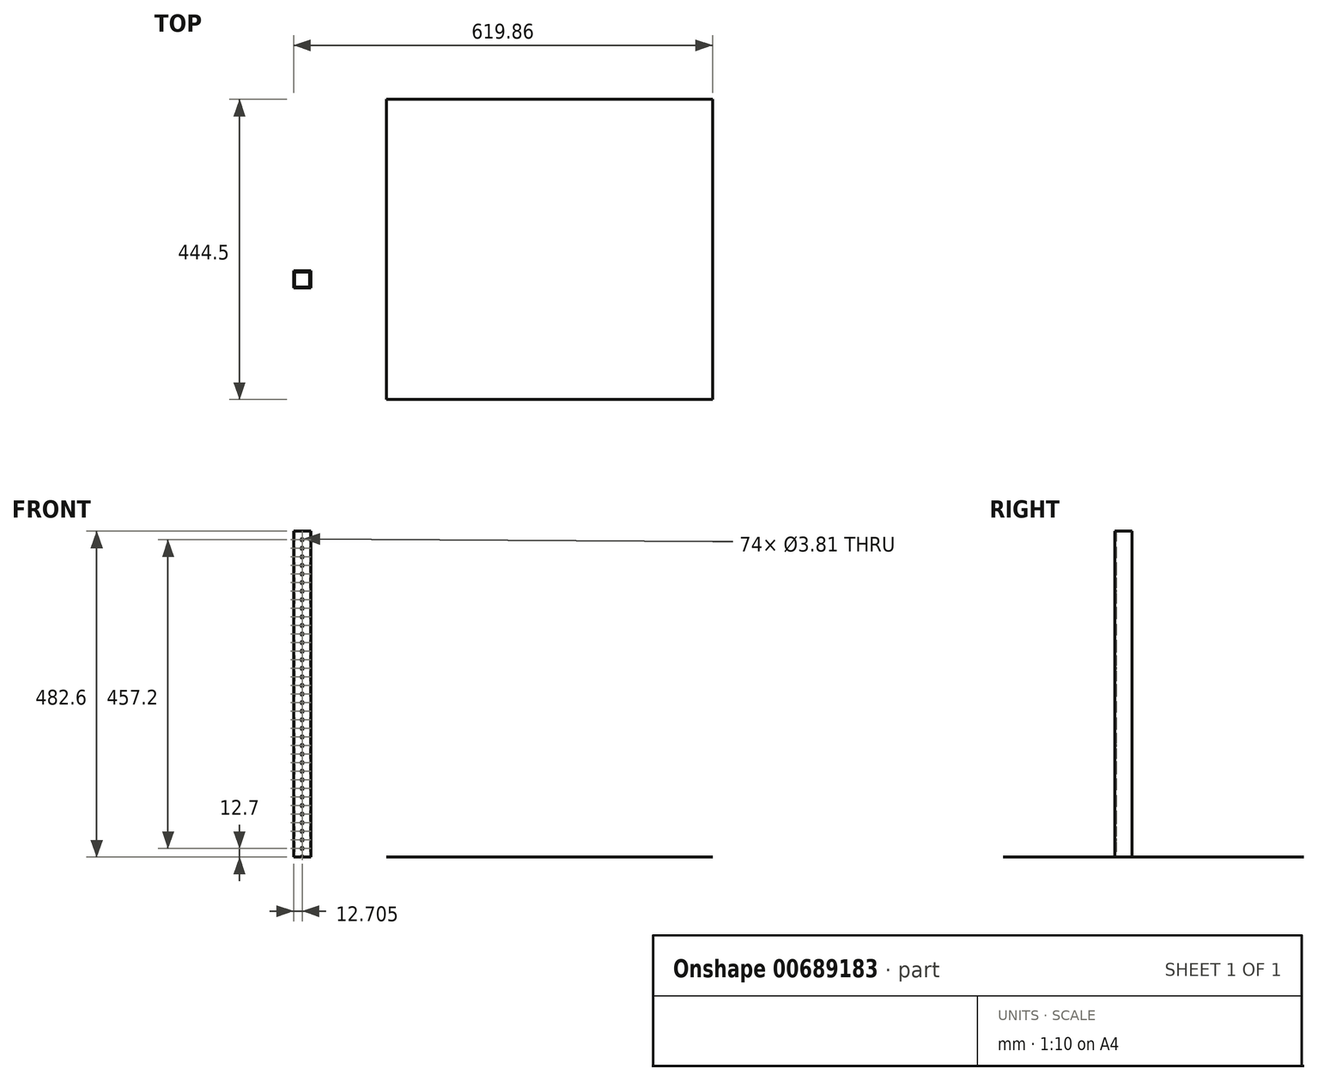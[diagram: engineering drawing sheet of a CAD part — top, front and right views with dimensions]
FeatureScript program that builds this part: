
annotation { "Feature Type Name" : "Feature", "Feature Type Description" : "" }
export const myFeature = defineFeature(function(context is Context, id is Id, definition is map)
    precondition{}
    {
        {
            var Q0;
            Q0=qCreatedBy(makeId("Top.planeOp"),FACE);
            var sketch = newSketch(context, id + "F0", { "sketchPlane" : qUnion([Q0])});
            skLineSegment(sketch, "E0.bottom", {"start": v(-66.34, 50.84) * mm, "end": v(-40.94, 50.84) * mm});
            skLineSegment(sketch, "E0.top", {"start": v(-66.34, 25.44) * mm, "end": v(-40.94, 25.44) * mm});
            skLineSegment(sketch, "E0.left", {"start": v(-66.34, 50.84) * mm, "end": v(-66.34, 25.44) * mm});
            skLineSegment(sketch, "E0.right", {"start": v(-40.94, 50.84) * mm, "end": v(-40.94, 25.44) * mm});
            skPoint(sketch, "E0.middle", {"position": v(-53.64, 38.14) * mm});
            skLineSegment(sketch, "E1.bottom", {"start": v(-64.75, 49.25) * mm, "end": v(-42.52, 49.25) * mm});
            skLineSegment(sketch, "E1.top", {"start": v(-64.75, 27.03) * mm, "end": v(-42.52, 27.03) * mm});
            skLineSegment(sketch, "E1.left", {"start": v(-64.75, 49.25) * mm, "end": v(-64.75, 27.03) * mm});
            skLineSegment(sketch, "E1.right", {"start": v(-42.52, 49.25) * mm, "end": v(-42.52, 27.03) * mm});
            skSolve(sketch);
        }
        {
            var Q0;
            Q0=makeQuery(id+"F0.imprint","IMPRINT",FACE,{"disambiguationData":[TD([[makeQuery(id+"F0.imprint","IMPRINT",EDGE,{"derivedFrom":sQuery(id+"F0.wireOp",EDGE,"E0.bottom")}),-1.0]])]});
            extrude(context, id + "F1", {"entities" : qUnion([Q0]), "depth" : 482.6 * mm, "offsetDistance" : 25.4 * mm});
        }
        {
            var Q0;
            Q0=makeQuery(id+"F1.opExtrude","SWEPT_FACE",FACE,{"disambiguationData":[OSD([sQuery(id+"F0.wireOp",EDGE,"E0.top")])]});
            var sketch = newSketch(context, id + "F2", { "sketchPlane" : qUnion([Q0])});
            skCircle(sketch, "E2", {"center": v(-53.64, 469.9) * mm, "radius": 1.9 * mm});
            skPoint(sketch, "E2.centerSnap0", {"position": v(-53.64, 482.6) * mm});
            skCircle(sketch, "E3.0.1.0", {"center": v(-53.64, 457.2) * mm, "radius": 1.9 * mm});
            skLineSegment(sketch, "E3.direction1", {"start": v(-53.64, 469.9) * mm, "end": v(-28.24, 469.9) * mm, "construction": true});
            skLineSegment(sketch, "E3.direction2", {"start": v(-53.64, 469.9) * mm, "end": v(-53.64, 457.2) * mm, "construction": true});
            skCircle(sketch, "E4.0.0.2", {"center": v(-53.64, 444.5) * mm, "radius": 1.9 * mm});
            skCircle(sketch, "E4.0.0.3", {"center": v(-53.64, 431.8) * mm, "radius": 1.9 * mm});
            skCircle(sketch, "E4.0.0.4", {"center": v(-53.64, 419.1) * mm, "radius": 1.9 * mm});
            skCircle(sketch, "E4.0.0.5", {"center": v(-53.64, 406.4) * mm, "radius": 1.9 * mm});
            skCircle(sketch, "E4.0.0.6", {"center": v(-53.64, 393.7) * mm, "radius": 1.9 * mm});
            skCircle(sketch, "E4.0.0.7", {"center": v(-53.64, 381) * mm, "radius": 1.9 * mm});
            skCircle(sketch, "E4.0.0.8", {"center": v(-53.64, 368.3) * mm, "radius": 1.9 * mm});
            skCircle(sketch, "E4.0.0.9", {"center": v(-53.64, 355.6) * mm, "radius": 1.9 * mm});
            skCircle(sketch, "E4.0.0.10", {"center": v(-53.64, 342.9) * mm, "radius": 1.9 * mm});
            skCircle(sketch, "E4.0.0.11", {"center": v(-53.64, 330.2) * mm, "radius": 1.9 * mm});
            skCircle(sketch, "E4.0.0.12", {"center": v(-53.64, 317.5) * mm, "radius": 1.9 * mm});
            skCircle(sketch, "E4.0.0.13", {"center": v(-53.64, 304.8) * mm, "radius": 1.9 * mm});
            skCircle(sketch, "E4.0.0.14", {"center": v(-53.64, 292.1) * mm, "radius": 1.9 * mm});
            skCircle(sketch, "E4.0.0.15", {"center": v(-53.64, 279.4) * mm, "radius": 1.9 * mm});
            skCircle(sketch, "E4.0.0.16", {"center": v(-53.64, 266.7) * mm, "radius": 1.9 * mm});
            skCircle(sketch, "E4.0.0.17", {"center": v(-53.64, 254) * mm, "radius": 1.9 * mm});
            skCircle(sketch, "E4.0.0.18", {"center": v(-53.64, 241.3) * mm, "radius": 1.9 * mm});
            skCircle(sketch, "E4.0.0.19", {"center": v(-53.64, 228.6) * mm, "radius": 1.9 * mm});
            skCircle(sketch, "E5.0.0.20", {"center": v(-53.64, 215.9) * mm, "radius": 1.9 * mm});
            skCircle(sketch, "E5.0.0.21", {"center": v(-53.64, 203.2) * mm, "radius": 1.9 * mm});
            skCircle(sketch, "E5.0.0.22", {"center": v(-53.64, 190.5) * mm, "radius": 1.9 * mm});
            skCircle(sketch, "E5.0.0.23", {"center": v(-53.64, 177.8) * mm, "radius": 1.9 * mm});
            skCircle(sketch, "E5.0.0.24", {"center": v(-53.64, 165.1) * mm, "radius": 1.9 * mm});
            skCircle(sketch, "E5.0.0.25", {"center": v(-53.64, 152.4) * mm, "radius": 1.9 * mm});
            skCircle(sketch, "E5.0.0.26", {"center": v(-53.64, 139.7) * mm, "radius": 1.9 * mm});
            skCircle(sketch, "E5.0.0.27", {"center": v(-53.64, 127) * mm, "radius": 1.9 * mm});
            skCircle(sketch, "E5.0.0.28", {"center": v(-53.64, 114.3) * mm, "radius": 1.9 * mm});
            skCircle(sketch, "E6.0.0.29", {"center": v(-53.64, 101.6) * mm, "radius": 1.9 * mm});
            skCircle(sketch, "E6.0.0.30", {"center": v(-53.64, 88.9) * mm, "radius": 1.9 * mm});
            skCircle(sketch, "E6.0.0.31", {"center": v(-53.64, 76.2) * mm, "radius": 1.9 * mm});
            skCircle(sketch, "E6.0.0.32", {"center": v(-53.64, 63.5) * mm, "radius": 1.9 * mm});
            skCircle(sketch, "E6.0.0.33", {"center": v(-53.64, 50.8) * mm, "radius": 1.9 * mm});
            skCircle(sketch, "E6.0.0.34", {"center": v(-53.64, 38.1) * mm, "radius": 1.9 * mm});
            skCircle(sketch, "E6.0.0.35", {"center": v(-53.64, 25.4) * mm, "radius": 1.9 * mm});
            skCircle(sketch, "E6.0.0.36", {"center": v(-53.64, 12.7) * mm, "radius": 1.9 * mm});
            skCircle(sketch, "E6.0.0.37", {"center": v(-53.64, 0) * mm, "radius": 1.9 * mm});
            skCircle(sketch, "E6.0.0.38", {"center": v(-53.64, -12.7) * mm, "radius": 1.9 * mm});
            skCircle(sketch, "E6.0.0.39", {"center": v(-53.64, -25.4) * mm, "radius": 1.9 * mm});
            skSolve(sketch);
        }
        {
            var Q0;
            Q0 = qSketchRegion(id + "F2", true);
            extrude(context, id + "F3", {"entities" : qUnion([Q0]), "operationType" : NewBodyOperationType.REMOVE, "endBound" : BoundingType.THROUGH_ALL, "oppositeDirection" : true, "depth" : 25.4 * mm, "offsetDistance" : 25.4 * mm});
        }
        {
            var Q0;
            Q0=qCreatedBy(makeId("Top.planeOp"),FACE);
            var sketch = newSketch(context, id + "F4", { "sketchPlane" : qUnion([Q0])});
            skLineSegment(sketch, "E7.bottom", {"start": v(70.92, 304.93) * mm, "end": v(553.52, 304.93) * mm});
            skLineSegment(sketch, "E7.top", {"start": v(70.92, -139.57) * mm, "end": v(553.52, -139.57) * mm});
            skLineSegment(sketch, "E7.left", {"start": v(70.92, 304.93) * mm, "end": v(70.92, -139.57) * mm});
            skLineSegment(sketch, "E7.right", {"start": v(553.52, 304.93) * mm, "end": v(553.52, -139.57) * mm});
            skPoint(sketch, "E7.middle", {"position": v(312.22, 82.68) * mm});
            skSolve(sketch);
        }
        {
            var Q0;
            Q0=makeQuery(id+"F4.imprint","IMPRINT",FACE,{"disambiguationData":[TD([[makeQuery(id+"F4.imprint","IMPRINT",EDGE,{"derivedFrom":sQuery(id+"F4.wireOp",EDGE,"E7.bottom")}),-1.0]])]});
            extrude(context, id + "F5", {"entities" : qUnion([Q0]), "depth" : 1 / 203.2 * mm, "offsetDistance" : 25.4 * mm});
        }
    });
